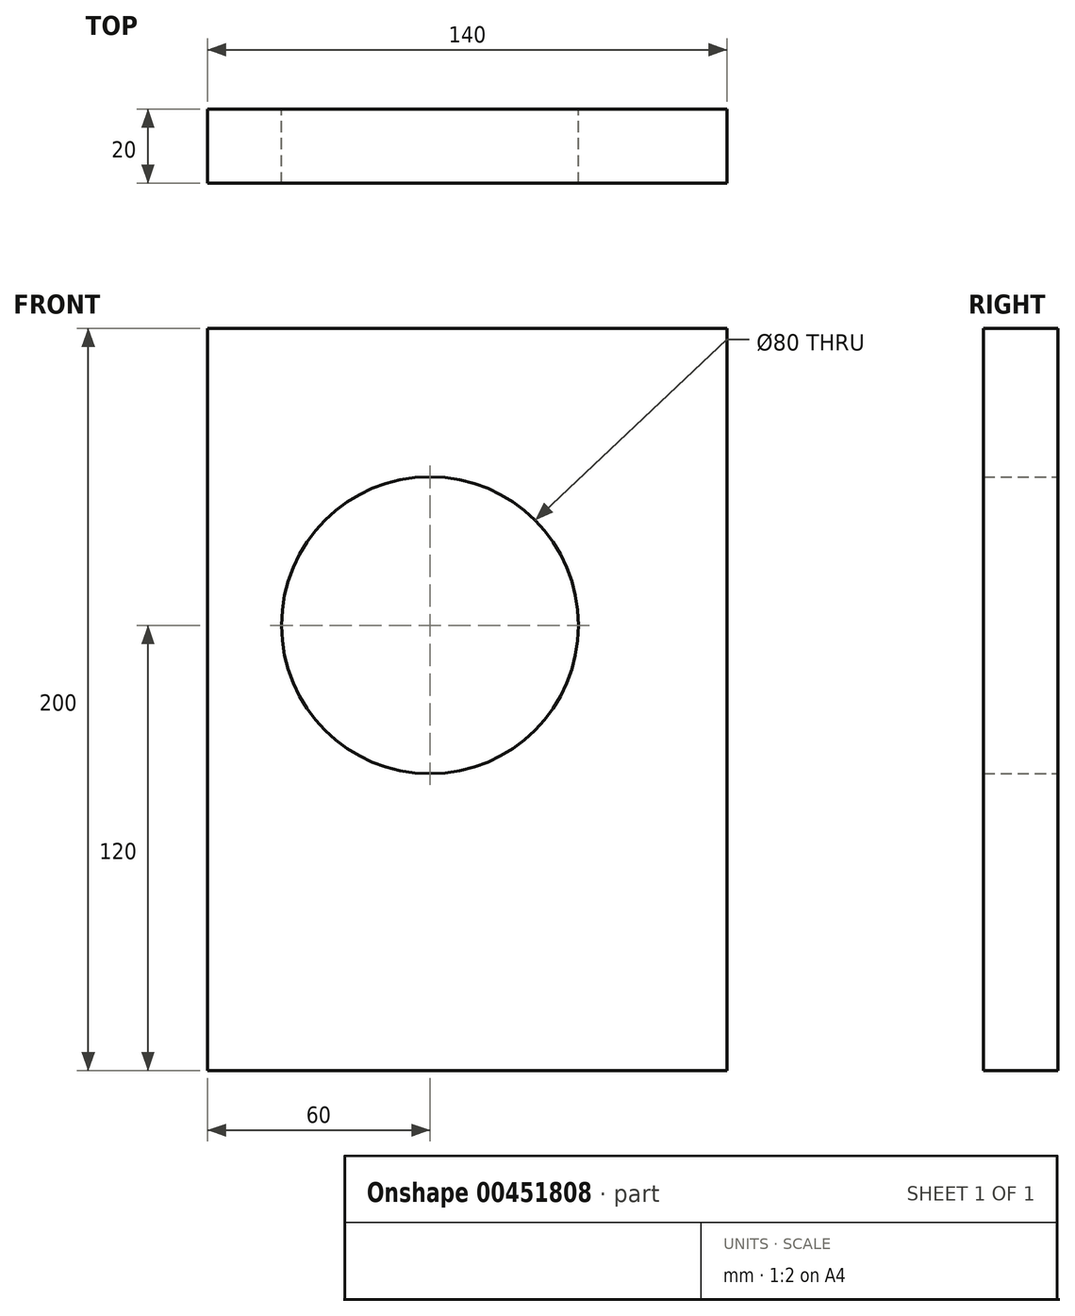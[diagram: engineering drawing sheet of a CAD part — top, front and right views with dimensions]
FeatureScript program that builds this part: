
annotation { "Feature Type Name" : "Feature", "Feature Type Description" : "" }
export const myFeature = defineFeature(function(context is Context, id is Id, definition is map)
    precondition{}
    {
        {
            var Q0;
            Q0=qCreatedBy(makeId("Front.planeOp"),FACE);
            var sketch = newSketch(context, id + "F0", { "sketchPlane" : qUnion([Q0])});
            skLineSegment(sketch, "E0.bottom", {"start": v(0, 0) * mm, "end": v(140, 0) * mm});
            skLineSegment(sketch, "E0.top", {"start": v(0, 200) * mm, "end": v(140, 200) * mm});
            skLineSegment(sketch, "E0.left", {"start": v(0, 0) * mm, "end": v(0, 200) * mm});
            skLineSegment(sketch, "E0.right", {"start": v(140, 0) * mm, "end": v(140, 200) * mm});
            skCircle(sketch, "E1", {"center": v(60, 120) * mm, "radius": 40 * mm});
            skSolve(sketch);
        }
        {
            var Q0;
            Q0=makeQuery(id+"F0.imprint","IMPRINT",FACE,{"disambiguationData":[TD([[makeQuery(id+"F0.imprint","IMPRINT",EDGE,{"derivedFrom":sQuery(id+"F0.wireOp",EDGE,"E0.bottom")}),1.0]])]});
            extrude(context, id + "F1", {"entities" : qUnion([Q0]), "endBound" : BoundingType.SYMMETRIC, "offsetDistance" : 25 * mm, "depth" : 20 * mm});
        }
    });
